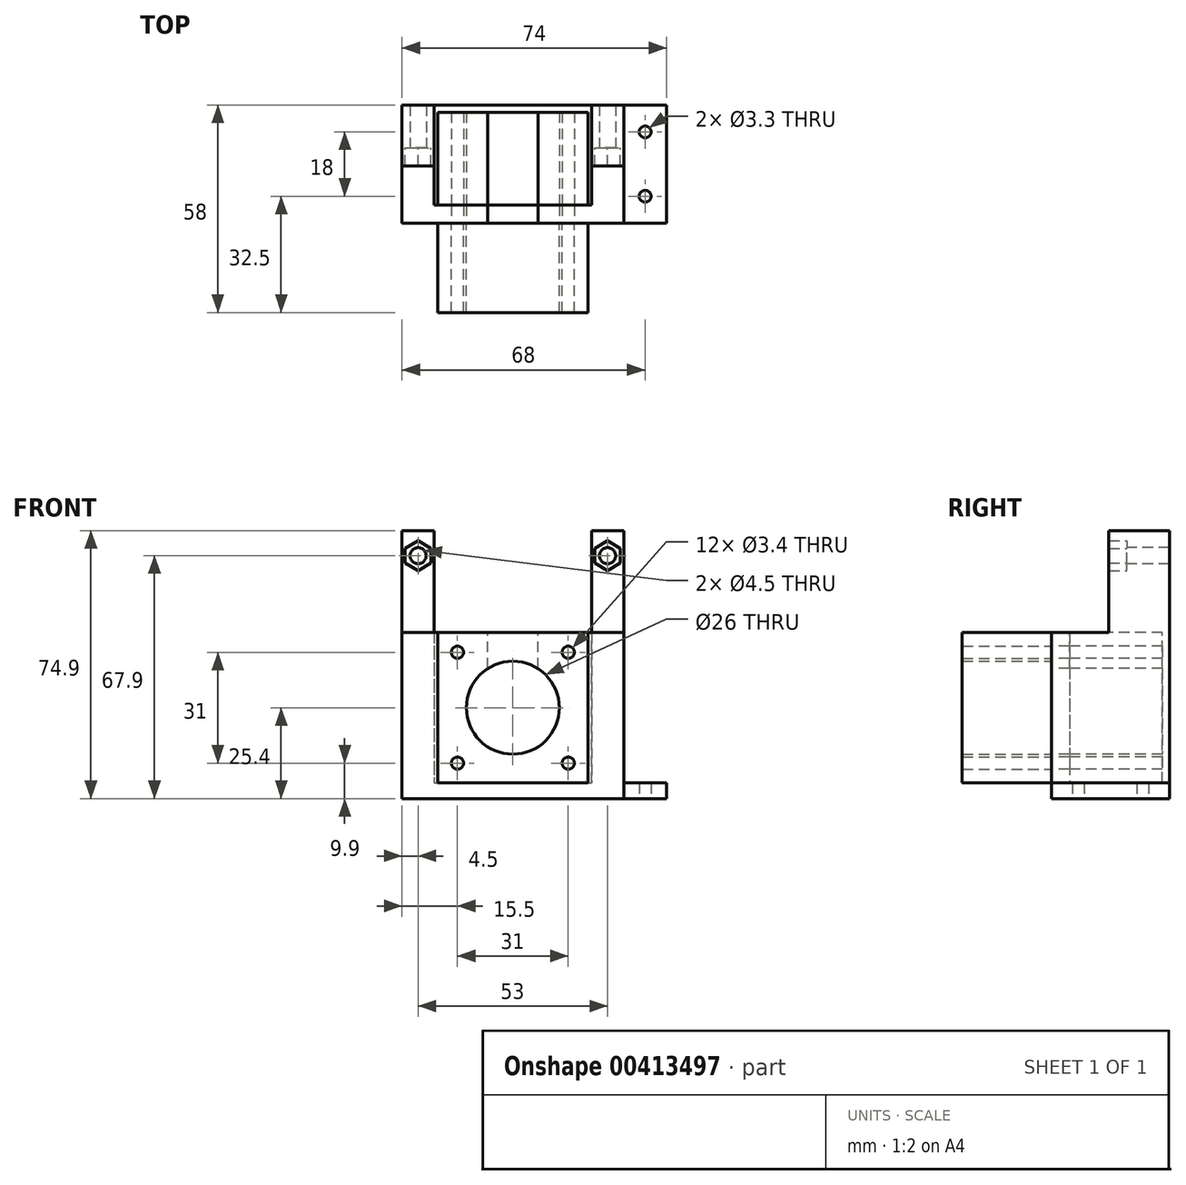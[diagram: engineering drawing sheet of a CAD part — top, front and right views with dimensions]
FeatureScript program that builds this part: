
annotation { "Feature Type Name" : "Feature", "Feature Type Description" : "" }
export const myFeature = defineFeature(function(context is Context, id is Id, definition is map)
    precondition{}
    {
        {
            assignVariable(context, id + "F0", {"name" : "MotorLength", "anyValue" : 26});
        }
        {
            var Q0;
            Q0=qCreatedBy(makeId("Front.planeOp"),FACE);
            var sketch = newSketch(context, id + "F1", { "sketchPlane" : qUnion([Q0])});
            skCircle(sketch, "E0", {"center": v(0, 0) * mm, "radius": 2.25 * mm});
            skCircle(sketch, "E1", {"center": v(-31.5, 49.5) * mm, "radius": 2.25 * mm});
            skCircle(sketch, "E2", {"center": v(21.5, 49.5) * mm, "radius": 2.25 * mm});
            skPoint(sketch, "E3", {"position": v(-36, 56.5) * mm});
            skPoint(sketch, "E4", {"position": v(-27, 56.5) * mm});
            skPoint(sketch, "E5", {"position": v(-27, -14) * mm});
            skLineSegment(sketch, "E6", {"start": v(-36, 56.5) * mm, "end": v(-27, 56.5) * mm});
            skLineSegment(sketch, "E7", {"start": v(-27, 56.5) * mm, "end": v(-27, -14) * mm});
            skLineSegment(sketch, "E8", {"start": v(-27, -14) * mm, "end": v(17, -14) * mm});
            skLineSegment(sketch, "E9", {"start": v(17, -14) * mm, "end": v(17, 56.5) * mm});
            skLineSegment(sketch, "E10", {"start": v(17, 56.5) * mm, "end": v(26, 56.5) * mm});
            skPoint(sketch, "E11", {"position": v(-36, -21) * mm});
            skLineSegment(sketch, "E12", {"start": v(-36, 56.5) * mm, "end": v(-36, -21) * mm});
            skLineSegment(sketch, "E13", {"start": v(-36, -21) * mm, "end": v(26, -21) * mm});
            skLineSegment(sketch, "E14", {"start": v(26, 56.5) * mm, "end": v(26, -21) * mm});
            skSolve(sketch);
        }
        {
            var Q0;
            Q0=makeQuery(id+"F1.imprint","IMPRINT",FACE,{"disambiguationData":[TD([[makeQuery(id+"F1.imprint","IMPRINT",EDGE,{"derivedFrom":sQuery(id+"F1.wireOp",EDGE,"E1")}),-1.0]])]});
            extrude(context, id + "F2", {"entities" : qUnion([Q0]), "oppositeDirection" : true, "depth" : 12 * mm});
        }
        {
            var Q0;
            Q0=makeQuery(id+"F2.opExtrude","CAP_FACE",FACE,{"disambiguationData":[OSD([sQuery(id+"F1.wireOp",EDGE,"E1"),sQuery(id+"F1.wireOp",EDGE,"E2"),sQuery(id+"F1.wireOp",EDGE,"E6"),sQuery(id+"F1.wireOp",EDGE,"E7"),sQuery(id+"F1.wireOp",EDGE,"E8"),sQuery(id+"F1.wireOp",EDGE,"E9"),sQuery(id+"F1.wireOp",EDGE,"E10"),sQuery(id+"F1.wireOp",EDGE,"E12"),sQuery(id+"F1.wireOp",EDGE,"E13"),sQuery(id+"F1.wireOp",EDGE,"E14")])],"isStart":true});
            var sketch = newSketch(context, id + "F3", { "sketchPlane" : qUnion([Q0])});
            skCircle(sketch, "E15.cCircle", {"center": v(-31.5, 49.5) * mm, "radius": 3.6 * mm, "construction": true});
            skLineSegment(sketch, "E15.0", {"start": v(-27.9, 51.58) * mm, "end": v(-27.9, 47.42) * mm});
            skLineSegment(sketch, "E15.1", {"start": v(-27.9, 47.42) * mm, "end": v(-31.5, 45.34) * mm});
            skLineSegment(sketch, "E15.2", {"start": v(-31.5, 45.34) * mm, "end": v(-35.1, 47.42) * mm});
            skLineSegment(sketch, "E15.3", {"start": v(-35.1, 47.42) * mm, "end": v(-35.1, 51.58) * mm});
            skLineSegment(sketch, "E15.4", {"start": v(-35.1, 51.58) * mm, "end": v(-31.5, 53.66) * mm});
            skLineSegment(sketch, "E15.5", {"start": v(-31.5, 53.66) * mm, "end": v(-27.9, 51.58) * mm});
            skPoint(sketch, "E15.0.midPoint", {"position": v(-27.9, 49.5) * mm});
            skCircle(sketch, "E16.cCircle", {"center": v(21.5, 49.5) * mm, "radius": 3.6 * mm, "construction": true});
            skLineSegment(sketch, "E16.0", {"start": v(25.1, 51.58) * mm, "end": v(25.1, 47.42) * mm});
            skLineSegment(sketch, "E16.1", {"start": v(25.1, 47.42) * mm, "end": v(21.5, 45.34) * mm});
            skLineSegment(sketch, "E16.2", {"start": v(21.5, 45.34) * mm, "end": v(17.9, 47.42) * mm});
            skLineSegment(sketch, "E16.3", {"start": v(17.9, 47.42) * mm, "end": v(17.9, 51.58) * mm});
            skLineSegment(sketch, "E16.4", {"start": v(17.9, 51.58) * mm, "end": v(21.5, 53.66) * mm});
            skLineSegment(sketch, "E16.5", {"start": v(21.5, 53.66) * mm, "end": v(25.1, 51.58) * mm});
            skPoint(sketch, "E16.0.midPoint", {"position": v(25.1, 49.5) * mm});
            skSolve(sketch);
        }
        {
            var Q0;
            Q0=makeQuery(id+"F3.imprint","IMPRINT",FACE,{"disambiguationData":[TD([[makeQuery(id+"F3.imprint","IMPRINT",EDGE,{"derivedFrom":sQuery(id+"F3.wireOp",EDGE,"E15.0")}),1.0]])]});
            extrude(context, id + "F4", {"entities" : qUnion([Q0]), "operationType" : NewBodyOperationType.ADD, "depth" : 5 * mm});
        }
        {
            var Q0;
            {var subQ0=sQuery(id+"F1.wireOp",EDGE,"E8");Q0=makeQuery(id+"F4.boolean.opBoolean","MERGE",FACE,{"derivedFrom":[makeQuery(id+"F2.opExtrude","SWEPT_FACE",FACE,{"disambiguationData":[OSD([subQ0])]}),makeQuery(id+"F4.opExtrude","SWEPT_FACE",FACE,{"disambiguationData":[OSD([subQ0])]})]});}
            var sketch = newSketch(context, id + "F5", { "sketchPlane" : qUnion([Q0])});
            skLineSegment(sketch, "E17.0", {"start": v(-27, 12) * mm, "end": v(17, 12) * mm});
            skPoint(sketch, "E18.oppositeSnap0", {"position": v(17, 3.5) * mm});
            skLineSegment(sketch, "E18.top", {"start": v(-27, -16) * mm, "end": v(17, -16) * mm});
            skLineSegment(sketch, "E18.left", {"start": v(-27, 12) * mm, "end": v(-27, -16) * mm});
            skLineSegment(sketch, "E18.right", {"start": v(17, 12) * mm, "end": v(17, -16) * mm});
            skLineSegment(sketch, "E19.top", {"start": v(-27, -21) * mm, "end": v(17, -21) * mm});
            skLineSegment(sketch, "E19.left", {"start": v(-27, -16) * mm, "end": v(-27, -21) * mm});
            skLineSegment(sketch, "E19.right", {"start": v(17, -16) * mm, "end": v(17, -21) * mm});
            skLineSegment(sketch, "E20.0", {"start": v(17, -5) * mm, "end": v(26, -5) * mm});
            skLineSegment(sketch, "E21.bottom", {"start": v(26, -5) * mm, "end": v(17, -5) * mm});
            skLineSegment(sketch, "E21.top", {"start": v(26, -21) * mm, "end": v(17, -21) * mm});
            skLineSegment(sketch, "E21.left", {"start": v(26, -5) * mm, "end": v(26, -21) * mm});
            skLineSegment(sketch, "E21.right", {"start": v(17, -5) * mm, "end": v(17, -21) * mm});
            skLineSegment(sketch, "E22.0", {"start": v(-36, -5) * mm, "end": v(-27, -5) * mm});
            skLineSegment(sketch, "E23.top", {"start": v(-36, -21) * mm, "end": v(-27, -21) * mm});
            skLineSegment(sketch, "E23.left", {"start": v(-36, -5) * mm, "end": v(-36, -21) * mm});
            skLineSegment(sketch, "E23.right", {"start": v(-27, -5) * mm, "end": v(-27, -21) * mm});
            skSolve(sketch);
        }
        {
            var Q0;
            {var subQ0=sQuery(id+"F5.wireOp",EDGE,"E18.top");Q0=makeQuery(id+"F5.imprint","IMPRINT",FACE,{"disambiguationData":[TD([[makeQuery(id+"F5.imprint","IMPRINT",EDGE,{"derivedFrom":subQ0}),1.0]])]});}
            var Q1;
            Q1=makeQuery(id+"F5.imprint","IMPRINT",FACE,{"disambiguationData":[TD([[makeQuery(id+"F5.imprint","IMPRINT",EDGE,{"derivedFrom":sQuery(id+"F5.wireOp",EDGE,"E18.top")}),-1.0]])]});
            var Q2;
            {var subQ2=sQuery(id+"F5.wireOp",EDGE,"E19.left");Q2=makeQuery(id+"F5.imprint","IMPRINT",FACE,{"disambiguationData":[TD([[makeQuery(id+"F5.imprint","IMPRINT",EDGE,{"derivedFrom":subQ2}),-1.0]])]});}
            var Q3;
            {var subQ0=sQuery(id+"F5.wireOp",EDGE,"E19.right");Q3=makeQuery(id+"F5.imprint","IMPRINT",FACE,{"disambiguationData":[TD([[makeQuery(id+"F5.imprint","IMPRINT",EDGE,{"derivedFrom":subQ0}),1.0]])]});}
            var Q4;
            {var subQ0=sQuery(id+"F1.wireOp",EDGE,"E13");Q4=makeQuery(id+"F4.boolean.opBoolean","MERGE",FACE,{"derivedFrom":[makeQuery(id+"F2.opExtrude","SWEPT_FACE",FACE,{"disambiguationData":[OSD([subQ0])]}),makeQuery(id+"F4.opExtrude","SWEPT_FACE",FACE,{"disambiguationData":[OSD([subQ0])]})]});}
            extrude(context, id + "F6", {"entities" : qUnion([Q0, Q1, Q2, Q3]), "operationType" : NewBodyOperationType.ADD, "endBound" : BoundingType.UP_TO_SURFACE, "oppositeDirection" : true, "endBoundEntityFace" : qUnion([Q4]), "depth" : 25 * mm});
        }
        {
            var Q0;
            Q0=makeQuery(id+"F5.imprint","IMPRINT",FACE,{"disambiguationData":[TD([[makeQuery(id+"F5.imprint","IMPRINT",EDGE,{"derivedFrom":sQuery(id+"F5.wireOp",EDGE,"E18.top")}),-1.0]])]});
            var Q1;
            {var subQ2=sQuery(id+"F5.wireOp",EDGE,"E19.left");Q1=makeQuery(id+"F5.imprint","IMPRINT",FACE,{"disambiguationData":[TD([[makeQuery(id+"F5.imprint","IMPRINT",EDGE,{"derivedFrom":subQ2}),-1.0]])]});}
            var Q2;
            {var subQ0=sQuery(id+"F5.wireOp",EDGE,"E19.right");Q2=makeQuery(id+"F5.imprint","IMPRINT",FACE,{"disambiguationData":[TD([[makeQuery(id+"F5.imprint","IMPRINT",EDGE,{"derivedFrom":subQ0}),1.0]])]});}
            extrude(context, id + "F7", {"entities" : qUnion([Q0, Q1, Q2]), "operationType" : NewBodyOperationType.ADD, "depth" : 42 * mm});
        }
        {
            var Q0;
            {var subQ0=sQuery(id+"F5.wireOp",EDGE,"E23.top");var subQ1=sQuery(id+"F5.wireOp",EDGE,"E21.top");var subQ2=sQuery(id+"F5.wireOp",EDGE,"E19.top");Q0=makeQuery(id+"F7.boolean.opBoolean","MERGE",FACE,{"derivedFrom":[makeQuery(id+"F6.opExtrude","SWEPT_FACE",FACE,{"disambiguationData":[OSD([subQ2,subQ1,subQ0])]}),makeQuery(id+"F7.opExtrude","SWEPT_FACE",FACE,{"disambiguationData":[OSD([subQ2,subQ1,subQ0])]})]});}
            var sketch = newSketch(context, id + "F8", { "sketchPlane" : qUnion([Q0])});
            skLineSegment(sketch, "E24.0", {"start": v(-26, -14) * mm, "end": v(16, -14) * mm});
            skPoint(sketch, "E25", {"position": v(-5, -14) * mm});
            skPoint(sketch, "E26", {"position": v(-26, -14) * mm});
            skPoint(sketch, "E27", {"position": v(16, -14) * mm});
            skPoint(sketch, "E28.orphan", {"position": v(-27, -14) * mm});
            skPoint(sketch, "E29.orphan", {"position": v(17, -14) * mm});
            skPoint(sketch, "E30", {"position": v(-26, 28) * mm});
            skPoint(sketch, "E31", {"position": v(16, 28) * mm});
            skLineSegment(sketch, "E32", {"start": v(-26, 28) * mm, "end": v(16, -14) * mm, "construction": true});
            skLineSegment(sketch, "E33", {"start": v(-26, -14) * mm, "end": v(16, 28) * mm, "construction": true});
            skPoint(sketch, "E34", {"position": v(-5, 7) * mm});
            skCircle(sketch, "E35", {"center": v(-5, 7) * mm, "radius": 13 * mm});
            skCircle(sketch, "E36", {"center": v(-20.5, 22.5) * mm, "radius": 1.7 * mm});
            skCircle(sketch, "E37.1.0", {"center": v(-20.5, -8.5) * mm, "radius": 1.7 * mm});
            skCircle(sketch, "E37.2.0", {"center": v(10.5, -8.5) * mm, "radius": 1.7 * mm});
            skCircle(sketch, "E37.3.0", {"center": v(10.5, 22.5) * mm, "radius": 1.7 * mm});
            skSolve(sketch);
        }
        {
            var Q0;
            Q0=makeQuery(id+"F8.imprint","IMPRINT",FACE,{"disambiguationData":[TD([[makeQuery(id+"F8.imprint","IMPRINT",EDGE,{"derivedFrom":sQuery(id+"F8.wireOp",EDGE,"E36")}),1.0]])]});
            var Q1;
            Q1=makeQuery(id+"F8.imprint","IMPRINT",FACE,{"disambiguationData":[TD([[makeQuery(id+"F8.imprint","IMPRINT",EDGE,{"derivedFrom":sQuery(id+"F8.wireOp",EDGE,"E35")}),1.0]])]});
            var Q2;
            Q2=makeQuery(id+"F8.imprint","IMPRINT",FACE,{"disambiguationData":[TD([[makeQuery(id+"F8.imprint","IMPRINT",EDGE,{"derivedFrom":sQuery(id+"F8.wireOp",EDGE,"E37.1.0")}),1.0]])]});
            var Q3;
            Q3=makeQuery(id+"F8.imprint","IMPRINT",FACE,{"disambiguationData":[TD([[makeQuery(id+"F8.imprint","IMPRINT",EDGE,{"derivedFrom":sQuery(id+"F8.wireOp",EDGE,"E37.2.0")}),1.0]])]});
            var Q4;
            Q4=makeQuery(id+"F8.imprint","IMPRINT",FACE,{"disambiguationData":[TD([[makeQuery(id+"F8.imprint","IMPRINT",EDGE,{"derivedFrom":sQuery(id+"F8.wireOp",EDGE,"E37.3.0")}),1.0]])]});
            var Q5;
            Q5=makeQuery(id+"F7.opExtrude","SWEPT_FACE",FACE,{"disambiguationData":[OSD([sQuery(id+"F5.wireOp",EDGE,"E18.top")])]});
            extrude(context, id + "F9", {"entities" : qUnion([Q0, Q1, Q2, Q3, Q4]), "operationType" : NewBodyOperationType.REMOVE, "endBound" : BoundingType.UP_TO_SURFACE, "oppositeDirection" : true, "endBoundEntityFace" : qUnion([Q5]), "depth" : 25 * mm});
        }
        {
            var Q0;
            Q0=makeQuery(id+"F7.opExtrude","CAP_FACE",FACE,{"disambiguationData":[OSD([sQuery(id+"F5.wireOp",EDGE,"E18.top"),sQuery(id+"F5.wireOp",EDGE,"E18.left"),sQuery(id+"F5.wireOp",EDGE,"E18.right"),sQuery(id+"F5.wireOp",EDGE,"E19.top"),sQuery(id+"F5.wireOp",EDGE,"E20.0"),sQuery(id+"F5.wireOp",EDGE,"E21.top"),sQuery(id+"F5.wireOp",EDGE,"E21.left"),sQuery(id+"F5.wireOp",EDGE,"E22.0"),sQuery(id+"F5.wireOp",EDGE,"E23.top"),sQuery(id+"F5.wireOp",EDGE,"E23.left")])],"isStart":false});
            var sketch = newSketch(context, id + "F10", { "sketchPlane" : qUnion([Q0])});
            skLineSegment(sketch, "E38", {"start": v(-5, -21) * mm, "end": v(-5, -16) * mm, "construction": true});
            skLineSegment(sketch, "E39", {"start": v(-5, -16) * mm, "end": v(-12, -16) * mm});
            skLineSegment(sketch, "E40", {"start": v(-5, -16) * mm, "end": v(2, -16) * mm});
            skLineSegment(sketch, "E41.bottom", {"start": v(-12, -16) * mm, "end": v(2, -16) * mm});
            skLineSegment(sketch, "E41.top", {"start": v(-12, -21) * mm, "end": v(2, -21) * mm});
            skLineSegment(sketch, "E41.left", {"start": v(-12, -16) * mm, "end": v(-12, -21) * mm});
            skLineSegment(sketch, "E41.right", {"start": v(2, -16) * mm, "end": v(2, -21) * mm});
            skSolve(sketch);
        }
        {
            var Q0;
            Q0=makeQuery(id+"F10.imprint","IMPRINT",FACE,{"disambiguationData":[TD([[makeQuery(id+"F10.imprint","IMPRINT",EDGE,{"derivedFrom":sQuery(id+"F10.wireOp",EDGE,"E41.top")}),1.0]])]});
            var Q1;
            Q1=makeQuery(id+"F9.boolean.opBoolean","COPY",FACE,{"derivedFrom":makeQuery(id+"F9.opExtrude","SWEPT_FACE",FACE,{"disambiguationData":[OSD([sQuery(id+"F8.wireOp",EDGE,"E35")])]})});
            extrude(context, id + "F11", {"entities" : qUnion([Q0]), "operationType" : NewBodyOperationType.REMOVE, "endBound" : BoundingType.UP_TO_SURFACE, "oppositeDirection" : true, "endBoundEntityFace" : qUnion([Q1]), "depth" : 25 * mm});
        }
        {
            var Q0;
            Q0=makeQuery(id+"F7.opExtrude","SWEPT_FACE",FACE,{"disambiguationData":[OSD([sQuery(id+"F5.wireOp",EDGE,"E18.top")])]});
            var sketch = newSketch(context, id + "F12", { "sketchPlane" : qUnion([Q0])});
            skLineSegment(sketch, "E42.0", {"start": v(26, -14) * mm, "end": v(-16, -14) * mm});
            skLineSegment(sketch, "E43", {"start": v(-16, -14) * mm, "end": v(-16, 28) * mm});
            skLineSegment(sketch, "E44", {"start": v(-16, 28) * mm, "end": v(26, 28) * mm});
            skLineSegment(sketch, "E45", {"start": v(26, 28) * mm, "end": v(26, -14) * mm});
            skSolve(sketch);
        }
        {
            var Q0;
            Q0=makeQuery(id+"F12.imprint","IMPRINT",FACE,{"disambiguationData":[TD([[makeQuery(id+"F12.imprint","IMPRINT",EDGE,{"derivedFrom":sQuery(id+"F12.wireOp",EDGE,"E42.0")}),-1.0]])]});
            var Q1;
            Q1=makeQuery(id+"F12.imprint","IMPRINT",FACE,{"disambiguationData":[TD([[makeQuery(id+"F12.imprint","IMPRINT",EDGE,{"derivedFrom":makeQuery(id+"F9.boolean.opBoolean","COPY",EDGE,{"derivedFrom":makeQuery(id+"F9.opExtrude","CAP_EDGE",EDGE,{"disambiguationData":[OSD([sQuery(id+"F8.wireOp",EDGE,"E35")])],"isStart":false})})}),-1.0]])]});
            var Q2;
            Q2=makeQuery(id+"F12.imprint","IMPRINT",FACE,{"disambiguationData":[TD([[makeQuery(id+"F12.imprint","IMPRINT",EDGE,{"derivedFrom":makeQuery(id+"F9.boolean.opBoolean","COPY",EDGE,{"derivedFrom":makeQuery(id+"F9.opExtrude","CAP_EDGE",EDGE,{"disambiguationData":[OSD([sQuery(id+"F8.wireOp",EDGE,"E36")])],"isStart":false})})}),-1.0]])]});
            var Q3;
            Q3=makeQuery(id+"F12.imprint","IMPRINT",FACE,{"disambiguationData":[TD([[makeQuery(id+"F12.imprint","IMPRINT",EDGE,{"derivedFrom":makeQuery(id+"F9.boolean.opBoolean","COPY",EDGE,{"derivedFrom":makeQuery(id+"F9.opExtrude","CAP_EDGE",EDGE,{"disambiguationData":[OSD([sQuery(id+"F8.wireOp",EDGE,"E37.3.0")])],"isStart":false})})}),-1.0]])]});
            var Q4;
            Q4=makeQuery(id+"F12.imprint","IMPRINT",FACE,{"disambiguationData":[TD([[makeQuery(id+"F12.imprint","IMPRINT",EDGE,{"derivedFrom":makeQuery(id+"F9.boolean.opBoolean","COPY",EDGE,{"derivedFrom":makeQuery(id+"F9.opExtrude","CAP_EDGE",EDGE,{"disambiguationData":[OSD([sQuery(id+"F8.wireOp",EDGE,"E37.2.0")])],"isStart":false})})}),-1.0]])]});
            var Q5;
            Q5=makeQuery(id+"F12.imprint","IMPRINT",FACE,{"disambiguationData":[TD([[makeQuery(id+"F12.imprint","IMPRINT",EDGE,{"derivedFrom":makeQuery(id+"F9.boolean.opBoolean","COPY",EDGE,{"derivedFrom":makeQuery(id+"F9.opExtrude","CAP_EDGE",EDGE,{"disambiguationData":[OSD([sQuery(id+"F8.wireOp",EDGE,"E37.1.0")])],"isStart":false})})}),-1.0]])]});
            extrude(context, id + "F13", {"entities" : qUnion([Q0, Q1, Q2, Q3, Q4, Q5]), "depth" : (getVariable(context, 'MotorLength')) * mm});
        }
        {
            var Q0;
            Q0=makeQuery(id+"F8.imprint","IMPRINT",FACE,{"disambiguationData":[TD([[makeQuery(id+"F8.imprint","IMPRINT",EDGE,{"derivedFrom":sQuery(id+"F8.wireOp",EDGE,"E35")}),-1.0]])]});
            var sketch = newSketch(context, id + "F14", { "sketchPlane" : qUnion([Q0])});
            skLineSegment(sketch, "E46.0", {"start": v(-26, 28) * mm, "end": v(16, -14) * mm, "construction": true});
            skLineSegment(sketch, "E47.0", {"start": v(-26, -14) * mm, "end": v(16, 28) * mm, "construction": true});
            skLineSegment(sketch, "E48.bottom", {"start": v(-26, 28) * mm, "end": v(16, 28) * mm});
            skLineSegment(sketch, "E48.top", {"start": v(-26, -14) * mm, "end": v(16, -14) * mm});
            skLineSegment(sketch, "E48.left", {"start": v(-26, 28) * mm, "end": v(-26, -14) * mm});
            skLineSegment(sketch, "E48.right", {"start": v(16, 28) * mm, "end": v(16, -14) * mm});
            skSolve(sketch);
        }
        {
            var Q0;
            Q0=makeQuery(id+"F14.imprint","IMPRINT",FACE,{"disambiguationData":[TD([[makeQuery(id+"F14.imprint","IMPRINT",EDGE,{"derivedFrom":sQuery(id+"F14.wireOp",EDGE,"E48.bottom")}),-1.0]])]});
            var Q1;
            Q1=makeQuery(id+"F8.imprint","IMPRINT",FACE,{"disambiguationData":[TD([[makeQuery(id+"F8.imprint","IMPRINT",EDGE,{"derivedFrom":sQuery(id+"F8.wireOp",EDGE,"E36")}),1.0]])]});
            var Q2;
            Q2=makeQuery(id+"F8.imprint","IMPRINT",FACE,{"disambiguationData":[TD([[makeQuery(id+"F8.imprint","IMPRINT",EDGE,{"derivedFrom":sQuery(id+"F8.wireOp",EDGE,"E35")}),1.0]])]});
            var Q3;
            Q3=makeQuery(id+"F8.imprint","IMPRINT",FACE,{"disambiguationData":[TD([[makeQuery(id+"F8.imprint","IMPRINT",EDGE,{"derivedFrom":sQuery(id+"F8.wireOp",EDGE,"E37.1.0")}),1.0]])]});
            var Q4;
            Q4=makeQuery(id+"F8.imprint","IMPRINT",FACE,{"disambiguationData":[TD([[makeQuery(id+"F8.imprint","IMPRINT",EDGE,{"derivedFrom":sQuery(id+"F8.wireOp",EDGE,"E37.3.0")}),1.0]])]});
            var Q5;
            Q5=makeQuery(id+"F8.imprint","IMPRINT",FACE,{"disambiguationData":[TD([[makeQuery(id+"F8.imprint","IMPRINT",EDGE,{"derivedFrom":sQuery(id+"F8.wireOp",EDGE,"E37.2.0")}),1.0]])]});
            extrude(context, id + "F15", {"entities" : qUnion([Q0, Q1, Q2, Q3, Q4, Q5]), "depth" : 25 * mm});
        }
        {
            var Q0;
            Q0=makeQuery(id+"F15.opExtrude","SWEPT_FACE",FACE,{"disambiguationData":[OSD([sQuery(id+"F14.wireOp",EDGE,"E48.top")])]});
            cPlane(context, id + "F16", {"entities" : qUnion([Q0]), "cplaneType" : CPlaneType.OFFSET, "offset" : 49 * mm, "width" : 150 * mm, "height" : 150 * mm});
        }
        {
            var Q0;
            Q0=qCreatedBy(id+"F16.planeOp",FACE);
            cPlane(context, id + "F17", {"entities" : qUnion([Q0]), "cplaneType" : CPlaneType.OFFSET, "offset" : 8.3 * mm, "oppositeDirection" : true, "width" : 150 * mm, "height" : 150 * mm});
        }
        {
            var Q0;
            Q0=qCreatedBy(id+"F17.planeOp",FACE);
            cPlane(context, id + "F18", {"entities" : qUnion([Q0]), "cplaneType" : CPlaneType.OFFSET, "offset" : 36.3 * mm, "oppositeDirection" : true, "width" : 150 * mm, "height" : 150 * mm});
        }
        {
            var Q0;
            {var subQ0=sQuery(id+"F1.wireOp",EDGE,"E13");Q0=makeQuery(id+"F6.boolean.opBoolean","MERGE",FACE,{"derivedFrom":[makeQuery(id+"F4.boolean.opBoolean","MERGE",FACE,{"derivedFrom":[makeQuery(id+"F2.opExtrude","SWEPT_FACE",FACE,{"disambiguationData":[OSD([subQ0])]}),makeQuery(id+"F4.opExtrude","SWEPT_FACE",FACE,{"disambiguationData":[OSD([subQ0])]})]}),makeQuery(id+"F6.opExtrude","CAP_FACE",FACE,{"disambiguationData":[OSD([sQuery(id+"F1.wireOp",EDGE,"E8"),sQuery(id+"F5.wireOp",EDGE,"E19.top"),sQuery(id+"F5.wireOp",EDGE,"E20.0"),sQuery(id+"F5.wireOp",EDGE,"E21.top"),sQuery(id+"F5.wireOp",EDGE,"E21.left"),sQuery(id+"F5.wireOp",EDGE,"E22.0"),sQuery(id+"F5.wireOp",EDGE,"E23.top"),sQuery(id+"F5.wireOp",EDGE,"E23.left")])],"isStart":false})]});}
            var Q1;
            Q1=qCreatedBy(id+"F18.planeOp",FACE);
            extrude(context, id + "F19", {"entities" : qUnion([Q0]), "operationType" : NewBodyOperationType.REMOVE, "endBound" : BoundingType.UP_TO_SURFACE, "oppositeDirection" : true, "endBoundEntityFace" : qUnion([Q1]), "depth" : 25 * mm});
        }
        {
            var Q0;
            Q0=makeQuery(id+"F19.boolean.opBoolean","COPY",FACE,{"derivedFrom":makeQuery(id+"F19.opExtrude","CAP_FACE",FACE,{"disambiguationData":[OSD([sQuery(id+"F1.wireOp",EDGE,"E8"),sQuery(id+"F1.wireOp",EDGE,"E13"),sQuery(id+"F5.wireOp",EDGE,"E19.top"),sQuery(id+"F5.wireOp",EDGE,"E20.0"),sQuery(id+"F5.wireOp",EDGE,"E21.top"),sQuery(id+"F5.wireOp",EDGE,"E21.left"),sQuery(id+"F5.wireOp",EDGE,"E22.0"),sQuery(id+"F5.wireOp",EDGE,"E23.top"),sQuery(id+"F5.wireOp",EDGE,"E23.left")])],"isStart":false})});
            var sketch = newSketch(context, id + "F20", { "sketchPlane" : qUnion([Q0])});
            skLineSegment(sketch, "E49.bottom", {"start": v(26, -12) * mm, "end": v(38, -12) * mm});
            skLineSegment(sketch, "E49.top", {"start": v(26, 21) * mm, "end": v(38, 21) * mm});
            skLineSegment(sketch, "E49.left", {"start": v(26, -12) * mm, "end": v(26, 21) * mm});
            skLineSegment(sketch, "E49.right", {"start": v(38, -12) * mm, "end": v(38, 21) * mm});
            skLineSegment(sketch, "E50", {"start": v(38, 4.5) * mm, "end": v(26, 4.5) * mm, "construction": true});
            skPoint(sketch, "E51", {"position": v(32, 4.5) * mm});
            skPoint(sketch, "E52", {"position": v(32, 13.5) * mm});
            skPoint(sketch, "E53.MirrorP", {"position": v(32, -4.5) * mm});
            skSolve(sketch);
        }
        {
            var Q0;
            Q0=makeQuery(id+"F20.imprint","IMPRINT",FACE,{"disambiguationData":[TD([[makeQuery(id+"F20.imprint","IMPRINT",EDGE,{"derivedFrom":sQuery(id+"F20.wireOp",EDGE,"E49.bottom")}),1.0]])]});
            var Q1;
            {var subQ0=sQuery(id+"F1.wireOp",EDGE,"E8");Q1=makeQuery(id+"F6.boolean.opBoolean","MERGE",FACE,{"derivedFrom":[makeQuery(id+"F4.boolean.opBoolean","MERGE",FACE,{"derivedFrom":[makeQuery(id+"F2.opExtrude","SWEPT_FACE",FACE,{"disambiguationData":[OSD([subQ0])]}),makeQuery(id+"F4.opExtrude","SWEPT_FACE",FACE,{"disambiguationData":[OSD([subQ0])]})]}),makeQuery(id+"F6.opExtrude","CAP_FACE",FACE,{"disambiguationData":[OSD([subQ0,sQuery(id+"F5.wireOp",EDGE,"E19.top"),sQuery(id+"F5.wireOp",EDGE,"E20.0"),sQuery(id+"F5.wireOp",EDGE,"E21.top"),sQuery(id+"F5.wireOp",EDGE,"E21.left"),sQuery(id+"F5.wireOp",EDGE,"E22.0"),sQuery(id+"F5.wireOp",EDGE,"E23.top"),sQuery(id+"F5.wireOp",EDGE,"E23.left")])],"isStart":true})]});}
            extrude(context, id + "F21", {"entities" : qUnion([Q0]), "endBound" : BoundingType.UP_TO_SURFACE, "oppositeDirection" : true, "endBoundEntityFace" : qUnion([Q1]), "depth" : 25 * mm});
        }
        {
            var Q0;
            Q0=sQuery(id+"F20.wireOp",VERTEX,"E53.MirrorP");
            var Q1;
            Q1=sQuery(id+"F20.wireOp",VERTEX,"E52");
            var Q2;
            Q2=makeQuery(id+"F21.opExtrude","SWEPT_BODY",BODY,{"disambiguationData":[OSD([sQuery(id+"F20.wireOp",EDGE,"E49.bottom"),sQuery(id+"F20.wireOp",EDGE,"E49.top"),sQuery(id+"F20.wireOp",EDGE,"E49.left"),sQuery(id+"F20.wireOp",EDGE,"E49.right")])]});
            hole(context, id + "F22", {"style" : HoleStyle.SIMPLE, "endStyle" : HoleEndStyle.THROUGH, "standardTappedOrClearance" : lookupTablePath({ "standard" : "ISO", "fit" : "Normal", "size" : "M3", "type" : "Clearance" }), "standardBlindInLast" : lookupTablePath({ "fit" : "Standard", "standard" : "ISO", "size" : "M3", "type" : "Clearance" }), "holeDiameter" : 3.3 * mm, "majorDiameter" : 5 * mm, "isTappedThrough" : true, "tappedDepth" : 12 * mm, "tapClearance" : 3, "startFromSketch" : true, "locations" : qUnion([Q0, Q1]), "scope" : qUnion([Q2])});
        }
    });
